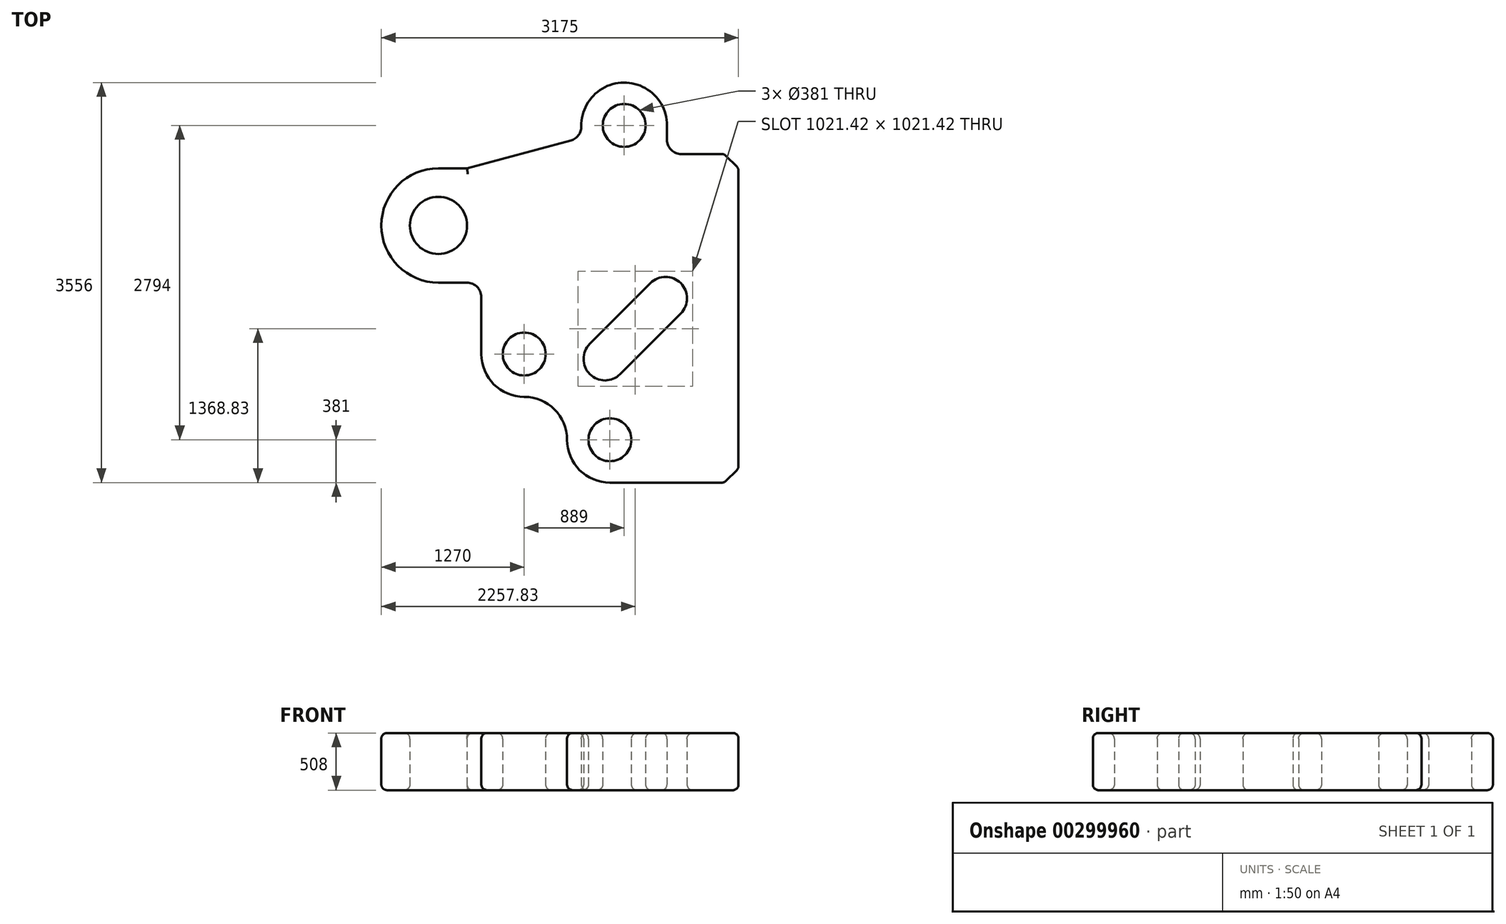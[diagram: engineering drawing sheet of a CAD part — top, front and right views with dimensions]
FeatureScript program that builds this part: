
annotation { "Feature Type Name" : "Feature", "Feature Type Description" : "" }
export const myFeature = defineFeature(function(context is Context, id is Id, definition is map)
    precondition{}
    {
        {
            var Q0;
            Q0=qCreatedBy(makeId("Top.planeOp"),FACE);
            var sketch = newSketch(context, id + "F0", { "sketchPlane" : qUnion([Q0])});
            skLineSegment(sketch, "E0", {"start": v(0, 0) * mm, "end": v(0, 2667) * mm});
            skPoint(sketch, "E1", {"position": v(-1143, -127) * mm});
            skLineSegment(sketch, "E2", {"start": v(-1143, -127) * mm, "end": v(-127, -127) * mm});
            skLineSegment(sketch, "E3", {"start": v(-127, -127) * mm, "end": v(0, 0) * mm});
            skArc(sketch, "E4", {"start": v(-1143, -127) * mm, "mid": v(-1412.4, -15.4) * mm, "end": v(-1524, 254) * mm});
            skArc(sketch, "E5", {"start": v(-1524, 254) * mm, "mid": v(-1635.6, 523.4) * mm, "end": v(-1905, 635) * mm});
            skArc(sketch, "E6", {"start": v(-1905, 635) * mm, "mid": v(-2174.4, 746.6) * mm, "end": v(-2286, 1016) * mm});
            skCircle(sketch, "E7", {"center": v(-1143, 254) * mm, "radius": 190.5 * mm});
            skCircle(sketch, "E8", {"center": v(-1905, 1016) * mm, "radius": 190.5 * mm});
            skPoint(sketch, "E9", {"position": v(-1186.58, 972.42) * mm});
            skArc(sketch, "E10", {"start": v(-1051.88, 837.72) * mm, "mid": v(-1321.28, 837.72) * mm, "end": v(-1321.28, 1107.12) * mm});
            skLineSegment(sketch, "E11", {"start": v(-1051.88, 837.72) * mm, "end": v(-513.06, 1376.53) * mm});
            skArc(sketch, "E12", {"start": v(-513.06, 1376.53) * mm, "mid": v(-513.06, 1645.94) * mm, "end": v(-782.47, 1645.94) * mm});
            skLineSegment(sketch, "E13", {"start": v(-1321.28, 1107.12) * mm, "end": v(-782.47, 1645.94) * mm});
            skPoint(sketch, "E14", {"position": v(-2667, 2159) * mm});
            skArc(sketch, "E15", {"start": v(-2667, 1651) * mm, "mid": v(-3175, 2159) * mm, "end": v(-2667, 2667) * mm});
            skCircle(sketch, "E16", {"center": v(-2667, 2159) * mm, "radius": 254 * mm});
            skLineSegment(sketch, "E17", {"start": v(-2667, 1651) * mm, "end": v(-2413, 1651) * mm});
            skLineSegment(sketch, "E18", {"start": v(-2286, 1016) * mm, "end": v(-2286, 1524) * mm});
            skArc(sketch, "E19", {"start": v(-2286, 1524) * mm, "mid": v(-2323.2, 1613.8) * mm, "end": v(-2413, 1651) * mm});
            skPoint(sketch, "E20", {"position": v(-1016, 3048) * mm});
            skCircle(sketch, "E21", {"center": v(-1016, 3048) * mm, "radius": 190.5 * mm});
            skArc(sketch, "E22", {"start": v(-635, 3048) * mm, "mid": v(-1020.23, 3428.98) * mm, "end": v(-1396.9, 3039.54) * mm});
            skArc(sketch, "E23", {"start": v(-635, 2921) * mm, "mid": v(-597.8, 2831.2) * mm, "end": v(-508, 2794) * mm});
            skLineSegment(sketch, "E24", {"start": v(-635, 3048) * mm, "end": v(-635, 2921) * mm});
            skPoint(sketch, "E25", {"position": v(-127, 2794) * mm});
            skLineSegment(sketch, "E26", {"start": v(-127, 2794) * mm, "end": v(0, 2667) * mm});
            skLineSegment(sketch, "E27", {"start": v(-127, 2794) * mm, "end": v(-508, 2794) * mm});
            skLineSegment(sketch, "E28", {"start": v(-2667, 2667) * mm, "end": v(-2413, 2667) * mm});
            skLineSegment(sketch, "E29", {"start": v(-2413, 2667) * mm, "end": v(-1936.23, 2667) * mm});
            skLineSegment(sketch, "E30", {"start": v(-2413, 2667) * mm, "end": v(-1491, 2914.05) * mm});
            skArc(sketch, "E31", {"start": v(-1396.9, 3039.54) * mm, "mid": v(-1422.27, 2960.53) * mm, "end": v(-1491, 2914.05) * mm});
            skLineSegment(sketch, "E32", {"start": v(-1905, 254) * mm, "end": v(-1186.58, 972.42) * mm});
            skSolve(sketch);
        }
        {
            var Q0;
            Q0 = qSketchRegion(id + "F0", true);
            extrude(context, id + "F1", {"entities" : qUnion([Q0]), "depth" : 508 * mm});
        }
        {
            var Q0;
            Q0=makeQuery(id+"F1.opExtrude","CAP_EDGE",EDGE,{"disambiguationData":[OSD([sQuery(id+"F0.wireOp",EDGE,"E15")])],"isStart":false});
            var Q1;
            Q1=makeQuery(id+"F1.opExtrude","CAP_EDGE",EDGE,{"disambiguationData":[OSD([sQuery(id+"F0.wireOp",EDGE,"E17")])],"isStart":false});
            var Q2;
            Q2=makeQuery(id+"F1.opExtrude","CAP_EDGE",EDGE,{"disambiguationData":[OSD([sQuery(id+"F0.wireOp",EDGE,"E19")])],"isStart":false});
            var Q3;
            Q3=makeQuery(id+"F1.opExtrude","CAP_EDGE",EDGE,{"disambiguationData":[OSD([sQuery(id+"F0.wireOp",EDGE,"E6")])],"isStart":true});
            var Q4;
            Q4=makeQuery(id+"F1.opExtrude","CAP_EDGE",EDGE,{"disambiguationData":[OSD([sQuery(id+"F0.wireOp",EDGE,"E3")])],"isStart":false});
            var Q5;
            Q5=makeQuery(id+"F1.opExtrude","CAP_EDGE",EDGE,{"disambiguationData":[OSD([sQuery(id+"F0.wireOp",EDGE,"E0")])],"isStart":false});
            var Q6;
            Q6=makeQuery(id+"F1.opExtrude","CAP_EDGE",EDGE,{"disambiguationData":[OSD([sQuery(id+"F0.wireOp",EDGE,"E26")])],"isStart":false});
            var Q7;
            Q7=makeQuery(id+"F1.opExtrude","CAP_EDGE",EDGE,{"disambiguationData":[OSD([sQuery(id+"F0.wireOp",EDGE,"E27")])],"isStart":false});
            var Q8;
            Q8=makeQuery(id+"F1.opExtrude","CAP_FACE",FACE,{"disambiguationData":[OSD([sQuery(id+"F0.wireOp",EDGE,"E0"),sQuery(id+"F0.wireOp",EDGE,"E2"),sQuery(id+"F0.wireOp",EDGE,"E3"),sQuery(id+"F0.wireOp",EDGE,"E4"),sQuery(id+"F0.wireOp",EDGE,"E5"),sQuery(id+"F0.wireOp",EDGE,"E6"),sQuery(id+"F0.wireOp",EDGE,"E7"),sQuery(id+"F0.wireOp",EDGE,"E8"),sQuery(id+"F0.wireOp",EDGE,"E10"),sQuery(id+"F0.wireOp",EDGE,"E11"),sQuery(id+"F0.wireOp",EDGE,"E12"),sQuery(id+"F0.wireOp",EDGE,"E13"),sQuery(id+"F0.wireOp",EDGE,"E15"),sQuery(id+"F0.wireOp",EDGE,"E16"),sQuery(id+"F0.wireOp",EDGE,"E17"),sQuery(id+"F0.wireOp",EDGE,"E18"),sQuery(id+"F0.wireOp",EDGE,"E19"),sQuery(id+"F0.wireOp",EDGE,"E21"),sQuery(id+"F0.wireOp",EDGE,"E22"),sQuery(id+"F0.wireOp",EDGE,"E23"),sQuery(id+"F0.wireOp",EDGE,"E24"),sQuery(id+"F0.wireOp",EDGE,"E26"),sQuery(id+"F0.wireOp",EDGE,"E27"),sQuery(id+"F0.wireOp",EDGE,"E28"),sQuery(id+"F0.wireOp",EDGE,"E30"),sQuery(id+"F0.wireOp",EDGE,"E31")])],"isStart":false});
            var Q9;
            Q9=makeQuery(id+"F1.opExtrude","CAP_FACE",FACE,{"disambiguationData":[OSD([sQuery(id+"F0.wireOp",EDGE,"E0"),sQuery(id+"F0.wireOp",EDGE,"E2"),sQuery(id+"F0.wireOp",EDGE,"E3"),sQuery(id+"F0.wireOp",EDGE,"E4"),sQuery(id+"F0.wireOp",EDGE,"E5"),sQuery(id+"F0.wireOp",EDGE,"E6"),sQuery(id+"F0.wireOp",EDGE,"E7"),sQuery(id+"F0.wireOp",EDGE,"E8"),sQuery(id+"F0.wireOp",EDGE,"E10"),sQuery(id+"F0.wireOp",EDGE,"E11"),sQuery(id+"F0.wireOp",EDGE,"E12"),sQuery(id+"F0.wireOp",EDGE,"E13"),sQuery(id+"F0.wireOp",EDGE,"E15"),sQuery(id+"F0.wireOp",EDGE,"E16"),sQuery(id+"F0.wireOp",EDGE,"E17"),sQuery(id+"F0.wireOp",EDGE,"E18"),sQuery(id+"F0.wireOp",EDGE,"E19"),sQuery(id+"F0.wireOp",EDGE,"E21"),sQuery(id+"F0.wireOp",EDGE,"E22"),sQuery(id+"F0.wireOp",EDGE,"E23"),sQuery(id+"F0.wireOp",EDGE,"E24"),sQuery(id+"F0.wireOp",EDGE,"E26"),sQuery(id+"F0.wireOp",EDGE,"E27"),sQuery(id+"F0.wireOp",EDGE,"E28"),sQuery(id+"F0.wireOp",EDGE,"E30"),sQuery(id+"F0.wireOp",EDGE,"E31")])],"isStart":true});
            var Q10;
            Q10=makeQuery(id+"F1.opExtrude","SWEPT_EDGE",EDGE,{"disambiguationData":[OSD([sQuery(id+"F0.wireOp",EDGE,"E2"),sQuery(id+"F0.wireOp",EDGE,"E3")])]});
            var Q11;
            Q11=makeQuery(id+"F1.opExtrude","SWEPT_EDGE",EDGE,{"disambiguationData":[OSD([sQuery(id+"F0.wireOp",EDGE,"E0"),sQuery(id+"F0.wireOp",EDGE,"E3")])]});
            var Q12;
            Q12=makeQuery(id+"F1.opExtrude","SWEPT_EDGE",EDGE,{"disambiguationData":[OSD([sQuery(id+"F0.wireOp",EDGE,"E0"),sQuery(id+"F0.wireOp",EDGE,"E26")])]});
            var Q13;
            Q13=makeQuery(id+"F1.opExtrude","SWEPT_EDGE",EDGE,{"disambiguationData":[OSD([sQuery(id+"F0.wireOp",EDGE,"E26"),sQuery(id+"F0.wireOp",EDGE,"E27")])]});
            fillet(context, id + "F2", {"entities" : qUnion([Q0, Q1, Q2, Q3, Q4, Q5, Q6, Q7, Q8, Q9, Q10, Q11, Q12, Q13]), "radius" : 50.8 * mm, "tangentPropagation" : true, "allowEdgeOverflow" : false});
        }
    });
